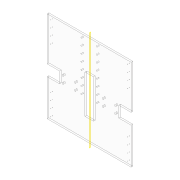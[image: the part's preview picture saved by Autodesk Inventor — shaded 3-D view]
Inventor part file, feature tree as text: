
AUTODESK INVENTOR PART (.ipt)
format: ipt  version: 2018 (Build 220112000, 112)  size: 186,368 bytes
history: native  units: in
note: dims shown in document units (in); Inventor stores cm internally (conversion verified against a paired STEP export)
features: reference x27, other x9, sketch x7, hole x4, extrude x3, mirror x2, plane x1
ambient origin geometry x8: Origin, YZ Plane, XZ Plane, XY Plane, X Axis, Y Axis, Z Axis, Center Point
bodies: Solid1 (feature_tree)
feature tree (53):
  extrude  "Extrusion1"  Depth=13.0in
  extrude  "Extrusion2"  Depth=0.25in
  plane  "Work Plane1"
  mirror  "Mirror1"
  hole  "Hole1"  [1 undecoded]
  hole  "Hole2"  [1 undecoded]
  mirror  "Mirror2"
  hole  "Hole3"  [1 undecoded]
  extrude  "Extrusion3"  [1 undecoded]
  hole  "Hole4"  [1 undecoded]
  sketch  "Sketch1"  dims[d0=12.0in d1=13.0in]
  sketch  "Sketch2"  dims[d2=0.25in d3=0.0in d4=0.7953in]
  sketch  "Sketch3"  dims[d5=0.7953in d6=1.0in d7=0.0in]
  reference  "Reference1"
  reference  "Reference2"
  reference  "Reference3"
  reference  "Reference4"
  reference  "Reference5"
  reference  "Reference6"
  reference  "Reference7"
  reference  "Reference8"
  sketch  "Sketch4"  dims[d8=0.25in d9=0.75in d10=0.375in d11=0.25in d12=0.5635in d13=1.0in d14=0.8108in]
  reference  "Reference9"
  reference  "Reference10"
  sketch  "Sketch5"  dims[d15=0.07in d16=0.5in d17=0.119in d18=0.25in d19=0.5635in d20=0.75in d21=0.8108in]
  reference  "Reference11"
  reference  "Reference12"
  sketch  "Sketch6"  dims[d22=0.177in d23=0.5in d24=0.332in d25=0.25in d26=0.5635in d27=0.75in d28=0.8108in d29=3.5in]
  reference  "Reference13"
  reference  "Reference14"
  reference  "Reference15"
  reference  "Reference16"
  reference  "Reference17"
  sketch  "Sketch8"  dims[d31=2.0in d32=1.0in d33=0.0in d36=0.177in d37=0.5in d38=0.332in d39=0.25in d40=0.5635in d41=0.75in d42=0.8108in]
  reference  "Reference21"
  reference  "Reference22"
  reference  "Reference23"
  reference  "Reference24"
  reference  "Reference25"
  reference  "Reference26"
  reference  "Reference27"
  reference  "Reference28"
  reference  "Reference29"
  reference  "Reference30"
  parser-record x1  (decoder bookkeeping rows leaked as tree rows — omitted from the tree; the rows remain in map.json)
  other  "Robot.iam"
  other  "VersaPlanetary_v2_Two_Stage_100_1_with_BAG:3"
  other  "VersaPlanetary_v2_Two_Stage_100_1_with_BAG:4"
  other  "Support Pivs 252:1"
  other  "Support Pivs 2522:2"
  other  "Support Pivs 2522:1"
  other  "Support Pivs 25 middle:1"
  other  "Support Pivs cross 2522:1"
note: 5 required parameter values undecoded (feature->parameter linkage not recoverable at this tier; creation-order binding heuristic only, values carry confidence <= 0.55)
note: 1 file-system path scrubbed to <path> (originals preserved in map.json)
